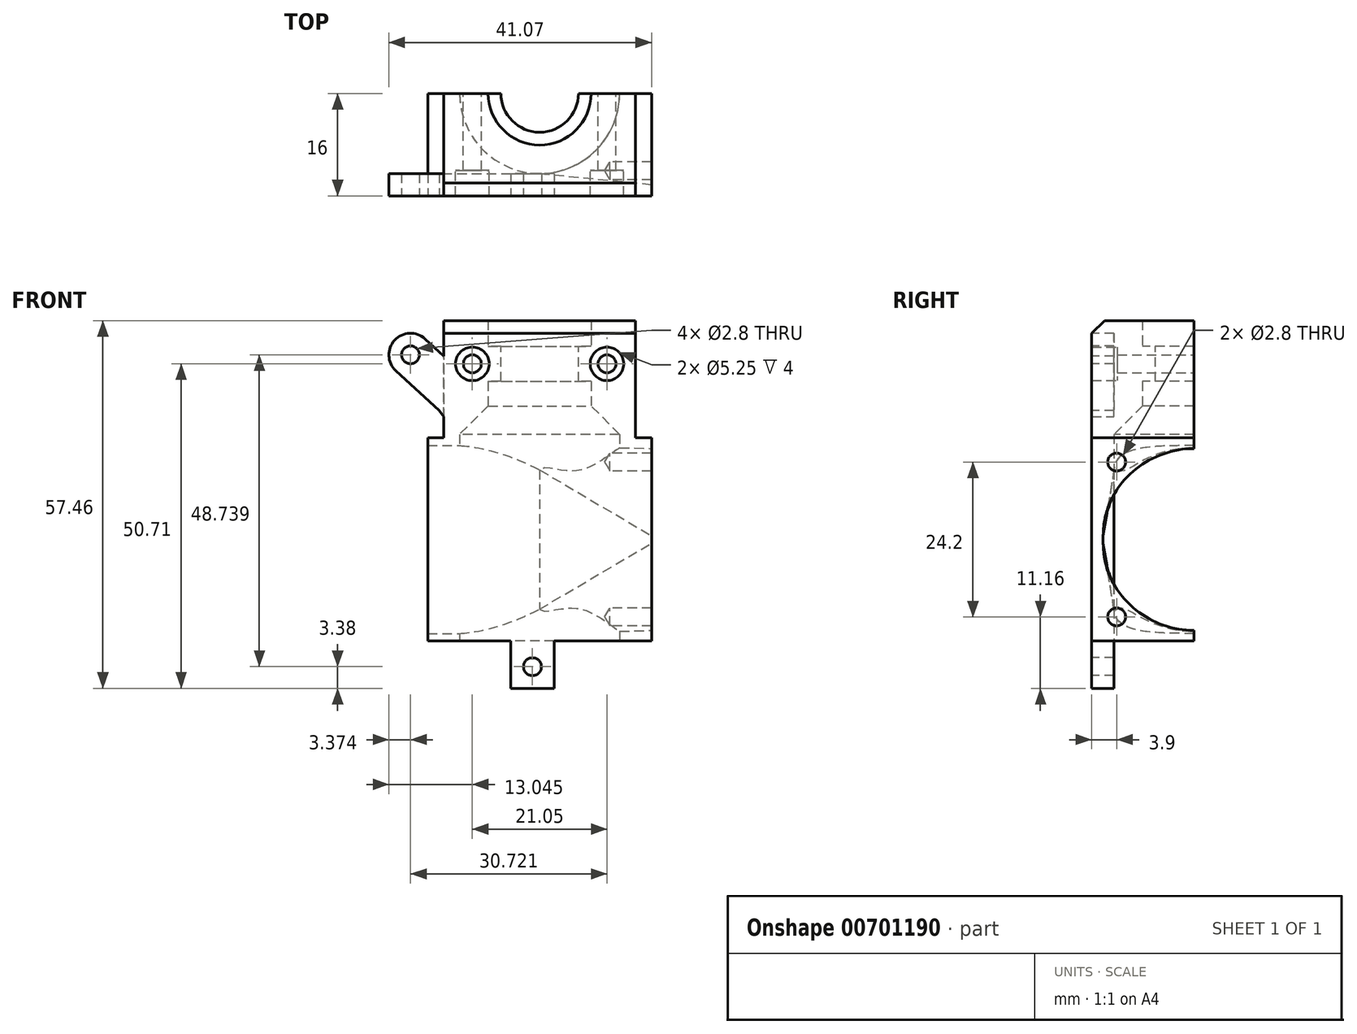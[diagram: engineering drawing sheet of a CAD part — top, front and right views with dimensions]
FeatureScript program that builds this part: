
annotation { "Feature Type Name" : "Feature", "Feature Type Description" : "" }
export const myFeature = defineFeature(function(context is Context, id is Id, definition is map)
    precondition{}
    {
        {
            var Q0;
            Q0=qCreatedBy(makeId("Front.planeOp"),FACE);
            var sketch = newSketch(context, id + "F0", { "sketchPlane" : qUnion([Q0])});
            skPoint(sketch, "E0.middle", {"position": v(0, 0) * mm});
            skLineSegment(sketch, "E1.bottom", {"start": v(17.5, 19.76) * mm, "end": v(-17.5, 19.76) * mm});
            skLineSegment(sketch, "E1.top", {"start": v(17.5, -12) * mm, "end": v(-17.5, -12) * mm});
            skLineSegment(sketch, "E1.left", {"start": v(17.5, 19.76) * mm, "end": v(17.5, -12) * mm});
            skLineSegment(sketch, "E1.right", {"start": v(-17.5, 19.76) * mm, "end": v(-17.5, -12) * mm});
            skLineSegment(sketch, "E2", {"start": v(-15, 19.76) * mm, "end": v(-15, 38.08) * mm});
            skLineSegment(sketch, "E3", {"start": v(-15, 38.08) * mm, "end": v(15, 38.08) * mm});
            skLineSegment(sketch, "E4", {"start": v(15, 38.08) * mm, "end": v(15, 19.76) * mm});
            skSolve(sketch);
        }
        {
            var Q0;
            Q0=makeQuery(id+"F0.imprint","IMPRINT",FACE,{"disambiguationData":[TD([[makeQuery(id+"F0.imprint","IMPRINT",EDGE,{"derivedFrom":sQuery(id+"F0.wireOp",EDGE,"E1.top")}),-1.0]])]});
            extrude(context, id + "F1", {"entities" : qUnion([Q0]), "oppositeDirection" : true, "depth" : 15 * mm, "offsetDistance" : 25 * mm});
        }
        {
            var Q0;
            Q0=makeQuery(id+"F1.opExtrude","SWEPT_FACE",FACE,{"disambiguationData":[OSD([sQuery(id+"F0.wireOp",EDGE,"E1.top")])]});
            var sketch = newSketch(context, id + "F2", { "sketchPlane" : qUnion([Q0])});
            skCircle(sketch, "E5", {"center": v(0, -15) * mm, "radius": 12.5 * mm});
            skSolve(sketch);
        }
        {
            var Q0;
            {var subQ0=sQuery(id+"F2.wireOp",EDGE,"E5");var subQ1=makeQuery(id+"F1.opExtrude","CAP_EDGE",EDGE,{"disambiguationData":[OSD([sQuery(id+"F0.wireOp",EDGE,"E1.top")])],"isStart":false});var subQ2=makeQuery(id+"F2.imprint","INTERSECT",VERTEX,{"disambiguationData":[OD(0.0)],"derivedFrom":[subQ1,subQ0]});Q0=makeQuery(id+"F2.imprint","IMPRINT",FACE,{"disambiguationData":[TD([[makeQuery(id+"F2.imprint","IMPRINT",EDGE,{"disambiguationData":[TD([[subQ2,-1.0]])],"derivedFrom":subQ0}),1.0]])]});}
            extrude(context, id + "F3", {"entities" : qUnion([Q0]), "operationType" : NewBodyOperationType.REMOVE, "endBound" : BoundingType.UP_TO_NEXT, "oppositeDirection" : true, "depth" : 25 * mm, "offsetDistance" : 25 * mm});
        }
        {
            var Q0;
            Q0=makeQuery(id+"F1.opExtrude","SWEPT_FACE",FACE,{"disambiguationData":[OSD([sQuery(id+"F0.wireOp",EDGE,"E1.right")])]});
            var sketch = newSketch(context, id + "F4", { "sketchPlane" : qUnion([Q0])});
            skFitSpline(sketch, "E6", {"points": [v(-15, -10.34) * mm, v(-0.79, 3.3) * mm], "startDerivative": vector(24.5, -0.23) * mm, "endDerivative": vector(0.56, 21.78) * mm});
            skFitSpline(sketch, "E7", {"points": [v(-15, 18.09) * mm, v(-0.79, 4.46) * mm], "startDerivative": vector(24.5, 0.26) * mm, "endDerivative": vector(0.56, -21.78) * mm});
            skLineSegment(sketch, "E8", {"start": v(-0.79, 4.46) * mm, "end": v(-0.79, 3.3) * mm});
            skLineSegment(sketch, "E9", {"start": v(-15, 3.88) * mm, "end": v(14.77, 3.88) * mm, "construction": true});
            skPoint(sketch, "E10", {"position": v(-2.9, 15.98) * mm});
            skPoint(sketch, "E11", {"position": v(-2.9, -8.22) * mm});
            skLineSegment(sketch, "E12", {"start": v(2.47, 18.88) * mm, "end": v(-9.32, 18.88) * mm, "construction": true});
            skLineSegment(sketch, "E13", {"start": v(1.95, -11.12) * mm, "end": v(-8.75, -11.12) * mm, "construction": true});
            skSolve(sketch);
        }
        {
            var Q0;
            Q0=makeQuery(id+"F1.opExtrude","SWEPT_FACE",FACE,{"disambiguationData":[OSD([sQuery(id+"F0.wireOp",EDGE,"E1.left")])]});
            var sketch = newSketch(context, id + "F5", { "sketchPlane" : qUnion([Q0])});
            skLineSegment(sketch, "E14", {"start": v(-4.6, 3.88) * mm, "end": v(19.4, 3.88) * mm, "construction": true});
            skLineSegment(sketch, "E15", {"start": v(-4.6, 18.88) * mm, "end": v(19.4, 18.88) * mm, "construction": true});
            skLineSegment(sketch, "E16", {"start": v(-4.6, -11.12) * mm, "end": v(19.4, -11.12) * mm, "construction": true});
            skLineSegment(sketch, "E17", {"start": v(0.79, 4.46) * mm, "end": v(0.79, 3.3) * mm});
            skFitSpline(sketch, "E18", {"points": [v(15, 18.1) * mm, v(0.79, 4.46) * mm], "startDerivative": vector(-21.58, 0) * mm, "endDerivative": vector(0, -24.08) * mm});
            skFitSpline(sketch, "E19", {"points": [v(0.79, 3.3) * mm, v(15, -10.33) * mm], "startDerivative": vector(0, -24.08) * mm, "endDerivative": vector(21.58, 0) * mm});
            skPoint(sketch, "E20", {"position": v(2.9, 15.98) * mm});
            skPoint(sketch, "E21", {"position": v(2.9, -8.22) * mm});
            skSolve(sketch);
        }
        {
            var Q0;
            {var subQ3=sQuery(id+"F4.wireOp",EDGE,"E6");Q0=makeQuery(id+"F4.imprint","IMPRINT",FACE,{"disambiguationData":[TD([[makeQuery(id+"F4.imprint","IMPRINT",EDGE,{"derivedFrom":subQ3}),-1.0]])]});}
            cPlane(context, id + "F6", {"entities" : qUnion([Q0]), "cplaneType" : CPlaneType.OFFSET, "offset" : 17.5 * mm, "oppositeDirection" : true, "width" : 150 * mm, "height" : 150 * mm});
        }
        {
            var Q0;
            Q0=qCreatedBy(id+"F6.planeOp",FACE);
            var sketch = newSketch(context, id + "F7", { "sketchPlane" : qUnion([Q0])});
            skFitSpline(sketch, "E22", {"points": [v(-15, -10.8) * mm, v(-2.5, -7) * mm], "startDerivative": vector(18.69, 0) * mm, "endDerivative": vector(0, 11.4) * mm});
            skLineSegment(sketch, "E23", {"start": v(-8.77, -11.88) * mm, "end": v(-8.77, 19.6) * mm, "construction": true});
            skFitSpline(sketch, "E24", {"points": [v(-15, 18.55) * mm, v(-2.5, 14.75) * mm], "startDerivative": vector(18.69, 0) * mm, "endDerivative": vector(0, -11.4) * mm});
            skLineSegment(sketch, "E25", {"start": v(-2.5, 20.58) * mm, "end": v(-2.5, -14.77) * mm, "construction": true});
            skLineSegment(sketch, "E26", {"start": v(-2.5, 14.75) * mm, "end": v(-2.5, -7) * mm});
            skLineSegment(sketch, "E27", {"start": v(-15, -10.8) * mm, "end": v(-15, 18.55) * mm});
            skSolve(sketch);
        }
        {
            var Q0;
            Q0=makeQuery(id+"F7.imprint","IMPRINT",FACE,{"disambiguationData":[TD([[makeQuery(id+"F7.imprint","IMPRINT",EDGE,{"derivedFrom":sQuery(id+"F7.wireOp",EDGE,"E22")}),1.0]])]});
            var Q1;
            Q1=makeQuery(id+"F5.imprint","IMPRINT",FACE,{"disambiguationData":[TD([[makeQuery(id+"F5.imprint","IMPRINT",EDGE,{"derivedFrom":sQuery(id+"F5.wireOp",EDGE,"E17")}),1.0]])]});
            loft(context, id + "F8", {"operationType" : NewBodyOperationType.REMOVE, "sheetProfilesArray" : [{ "sheetProfileEntities" : qUnion([Q0]) }, { "sheetProfileEntities" : qUnion([Q1]) }]});
        }
        {
            var Q0;
            Q0=qSketchRegion(id+"F7",true);
            extrude(context, id + "F9", {"entities" : qUnion([Q0]), "operationType" : NewBodyOperationType.REMOVE, "depth" : 30 * mm, "offsetDistance" : 25 * mm});
        }
        {
            var Q0;
            Q0=qSketchRegion(id+"F0",true);
            extrude(context, id + "F10", {"entities" : qUnion([Q0]), "operationType" : NewBodyOperationType.ADD, "depth" : 1 * mm, "offsetDistance" : 25 * mm});
        }
        {
            var Q0;
            Q0=sQuery(id+"F5.wireOp",VERTEX,"E20");
            var Q1;
            Q1=sQuery(id+"F5.wireOp",VERTEX,"E21");
            var Q2;
            Q2=makeQuery(id+"F1.opExtrude","SWEPT_BODY",BODY,{"disambiguationData":[OSD([sQuery(id+"F0.wireOp",EDGE,"olvQiCSQ-iVDM-BvRe-21EI-2ykU3FyUineD"),sQuery(id+"F0.wireOp",EDGE,"tQqsZeP7-s7as-o93x-ybZ7-DSYlx5VF5dZE"),sQuery(id+"F0.wireOp",EDGE,"E1.bottom"),sQuery(id+"F0.wireOp",EDGE,"E1.top"),sQuery(id+"F0.wireOp",EDGE,"E1.left"),sQuery(id+"F0.wireOp",EDGE,"E1.right")])]});
            hole(context, id + "F11", {"style" : HoleStyle.SIMPLE, "endStyle" : HoleEndStyle.BLIND, "holeDiameter" : 2.8 * mm, "majorDiameter" : 5 * mm, "holeDepth" : 6.5 * mm, "isTappedThrough" : true, "tappedDepth" : 12 * mm, "tapClearance" : 3, "locations" : qUnion([Q0, Q1]), "scope" : qUnion([Q2]), "startStyle" : HoleStartStyle.PART});
        }
        {
            var Q0;
            Q0=makeQuery(id+"F10.opExtrude","SWEPT_FACE",FACE,{"disambiguationData":[OSD([sQuery(id+"F0.wireOp",EDGE,"E3")])]});
            cPlane(context, id + "F12", {"entities" : qUnion([Q0]), "cplaneType" : CPlaneType.OFFSET, "offset" : 18.32 * mm, "oppositeDirection" : true, "width" : 150 * mm, "height" : 150 * mm});
        }
        {
            var Q0;
            Q0=qCreatedBy(id+"F12.planeOp",FACE);
            var sketch = newSketch(context, id + "F13", { "sketchPlane" : qUnion([Q0])});
            skLineSegment(sketch, "E28.bottom", {"start": v(-15, 0) * mm, "end": v(15, 0) * mm});
            skLineSegment(sketch, "E28.top", {"start": v(-15, 15) * mm, "end": v(15, 15) * mm});
            skLineSegment(sketch, "E28.left", {"start": v(-15, 0) * mm, "end": v(-15, 15) * mm});
            skLineSegment(sketch, "E28.right", {"start": v(15, 0) * mm, "end": v(15, 15) * mm});
            skCircle(sketch, "E29", {"center": v(0, 15) * mm, "radius": 8.05 * mm});
            skCircle(sketch, "E30", {"center": v(0, 15) * mm, "radius": 6.05 * mm});
            skSolve(sketch);
        }
        {
            var Q0;
            Q0=makeQuery(id+"F13.imprint","IMPRINT",FACE,{"disambiguationData":[TD([[makeQuery(id+"F13.imprint","IMPRINT",EDGE,{"derivedFrom":sQuery(id+"F13.wireOp",EDGE,"E28.bottom")}),1.0]])]});
            extrude(context, id + "F14", {"entities" : qUnion([Q0]), "operationType" : NewBodyOperationType.ADD, "depth" : 18.32 * mm, "offsetDistance" : 25 * mm});
        }
        {
            var Q0;
            Q0=makeQuery(id+"F14.boolean.opBoolean","MERGE",FACE,{"derivedFrom":[makeQuery(id+"F10.opExtrude","SWEPT_FACE",FACE,{"disambiguationData":[OSD([sQuery(id+"F0.wireOp",EDGE,"E3")])]}),makeQuery(id+"F14.opExtrude","CAP_FACE",FACE,{"disambiguationData":[OSD([sQuery(id+"F13.wireOp",EDGE,"E28.bottom"),sQuery(id+"F13.wireOp",EDGE,"E28.top"),sQuery(id+"F13.wireOp",EDGE,"E28.left"),sQuery(id+"F13.wireOp",EDGE,"E28.right"),sQuery(id+"F13.wireOp",EDGE,"E29")])],"isStart":false})]});
            cPlane(context, id + "F15", {"entities" : qUnion([Q0]), "cplaneType" : CPlaneType.OFFSET, "offset" : 4 * mm, "oppositeDirection" : true, "width" : 150 * mm, "height" : 150 * mm});
        }
        {
            var Q0;
            Q0=qCreatedBy(id+"F15.planeOp",FACE);
            var sketch = newSketch(context, id + "F16", { "sketchPlane" : qUnion([Q0])});
            skCircle(sketch, "E31", {"center": v(0, 15) * mm, "radius": 6.05 * mm});
            skCircle(sketch, "E32", {"center": v(0, 15) * mm, "radius": 8.05 * mm});
            skLineSegment(sketch, "E33", {"start": v(0, 0) * mm, "end": v(12, 0) * mm});
            skLineSegment(sketch, "E34", {"start": v(12, 0) * mm, "end": v(12, 15) * mm});
            skLineSegment(sketch, "E35", {"start": v(12, 15) * mm, "end": v(-12, 15) * mm});
            skLineSegment(sketch, "E36", {"start": v(-12, 15) * mm, "end": v(-12, 0) * mm});
            skLineSegment(sketch, "E37", {"start": v(-12, 0) * mm, "end": v(0, 0) * mm});
            skSolve(sketch);
        }
        {
            var Q0;
            {var subQ0=sQuery(id+"F16.wireOp",EDGE,"E35");var subQ1=sQuery(id+"F16.wireOp",EDGE,"E31");var subQ2=makeQuery(id+"F16.imprint","INTERSECT",VERTEX,{"disambiguationData":[OD(0.0)],"derivedFrom":[subQ1,subQ0]});Q0=makeQuery(id+"F16.imprint","IMPRINT",FACE,{"disambiguationData":[TD([[makeQuery(id+"F16.imprint","IMPRINT",EDGE,{"disambiguationData":[TD([[subQ2,1.0]])],"derivedFrom":subQ1}),-1.0]])]});}
            extrude(context, id + "F17", {"entities" : qUnion([Q0]), "operationType" : NewBodyOperationType.ADD, "oppositeDirection" : true, "depth" : 5.5 * mm, "offsetDistance" : 25 * mm});
        }
        {
            var Q0;
            Q0=makeQuery(id+"F10.opExtrude","CAP_FACE",FACE,{"disambiguationData":[OSD([sQuery(id+"F0.wireOp",EDGE,"E1.top"),sQuery(id+"F0.wireOp",EDGE,"E1.left"),sQuery(id+"F0.wireOp",EDGE,"E1.right"),sQuery(id+"F0.wireOp",EDGE,"E1.bottom"),sQuery(id+"F0.wireOp",EDGE,"E2"),sQuery(id+"F0.wireOp",EDGE,"E3"),sQuery(id+"F0.wireOp",EDGE,"E4")])],"isStart":false});
            var sketch = newSketch(context, id + "F18", { "sketchPlane" : qUnion([Q0])});
            skPoint(sketch, "E38", {"position": v(10.52, 31.33) * mm});
            skPoint(sketch, "E39", {"position": v(-10.53, 31.33) * mm});
            skLineSegment(sketch, "E40", {"start": v(15, 31.33) * mm, "end": v(6.05, 31.33) * mm, "construction": true});
            skLineSegment(sketch, "E41", {"start": v(-15, 31.33) * mm, "end": v(-6.05, 31.33) * mm, "construction": true});
            skSolve(sketch);
        }
        {
            var Q0;
            Q0=sQuery(id+"F18.wireOp",VERTEX,"E38");
            var Q1;
            Q1=sQuery(id+"F18.wireOp",VERTEX,"E39");
            var Q2;
            Q2=makeQuery(id+"F1.opExtrude","SWEPT_BODY",BODY,{"disambiguationData":[OSD([sQuery(id+"F0.wireOp",EDGE,"olvQiCSQ-iVDM-BvRe-21EI-2ykU3FyUineD"),sQuery(id+"F0.wireOp",EDGE,"tQqsZeP7-s7as-o93x-ybZ7-DSYlx5VF5dZE"),sQuery(id+"F0.wireOp",EDGE,"E1.top"),sQuery(id+"F0.wireOp",EDGE,"E1.left"),sQuery(id+"F0.wireOp",EDGE,"E1.right"),sQuery(id+"F0.wireOp",EDGE,"E1.bottom")])]});
            hole(context, id + "F19", {"style" : HoleStyle.C_BORE, "endStyle" : HoleEndStyle.BLIND, "holeDiameter" : 2.8 * mm, "cBoreDiameter" : 5.25 * mm, "cBoreDepth" : 4 * mm, "majorDiameter" : 5 * mm, "holeDepth" : 20 * mm, "isTappedThrough" : true, "tappedDepth" : 12 * mm, "tapClearance" : 3, "locations" : qUnion([Q0, Q1]), "scope" : qUnion([Q2]), "startStyle" : HoleStartStyle.PART});
        }
        {
            var Q0;
            Q0=makeQuery(id+"F10.opExtrude","CAP_EDGE",EDGE,{"disambiguationData":[OSD([sQuery(id+"F0.wireOp",EDGE,"E3")])],"isStart":false});
            chamfer(context, id + "F20", {"entities" : qUnion([Q0]), "width" : 2 * mm, "tangentPropagation" : true});
        }
        {
            var Q0;
            Q0=makeQuery(id+"F14.opExtrude","CAP_EDGE",EDGE,{"disambiguationData":[OSD([sQuery(id+"F13.wireOp",EDGE,"E29")])],"isStart":true});
            var Q1;
            Q1=makeQuery(id+"F14.opExtrude","CAP_EDGE",EDGE,{"disambiguationData":[OSD([sQuery(id+"F13.wireOp",EDGE,"E28.right")])],"isStart":true});
            var Q2;
            Q2=makeQuery(id+"F14.opExtrude","CAP_EDGE",EDGE,{"disambiguationData":[OSD([sQuery(id+"F13.wireOp",EDGE,"E28.left")])],"isStart":true});
            chamfer(context, id + "F21", {"entities" : qUnion([Q0, Q1, Q2]), "width" : 5 * mm, "tangentPropagation" : true});
        }
        {
            var Q0;
            Q0=makeQuery(id+"F18.imprint","IMPRINT",FACE,{"disambiguationData":[TD([[makeQuery(id+"F18.imprint","IMPRINT",EDGE,{"derivedFrom":makeQuery(id+"F10.opExtrude","CAP_EDGE",EDGE,{"disambiguationData":[OSD([sQuery(id+"F0.wireOp",EDGE,"E1.top")])],"isStart":false})}),-1.0]])]});
            var sketch = newSketch(context, id + "F22", { "sketchPlane" : qUnion([Q0])});
            skLineSegment(sketch, "E42", {"start": v(-15, 32.56) * mm, "end": v(-17.92, 35.23) * mm});
            skLineSegment(sketch, "E43", {"start": v(-22.47, 30.25) * mm, "end": v(-15.7, 24.06) * mm});
            skCircle(sketch, "E44", {"center": v(-20.2, 32.74) * mm, "radius": 3.37 * mm});
            skPoint(sketch, "E44.third.point", {"position": v(-22.47, 35.23) * mm});
            skCircle(sketch, "E45", {"center": v(-20.2, 32.74) * mm, "radius": 1.4 * mm});
            skLineSegment(sketch, "E46.bottom", {"start": v(2.25, -12) * mm, "end": v(-4.5, -12) * mm});
            skLineSegment(sketch, "E46.top", {"start": v(2.25, -16) * mm, "end": v(-4.5, -16) * mm});
            skLineSegment(sketch, "E46.left", {"start": v(2.25, -12) * mm, "end": v(2.25, -16) * mm});
            skLineSegment(sketch, "E46.right", {"start": v(-4.5, -12) * mm, "end": v(-4.5, -16) * mm});
            skCircle(sketch, "E47", {"center": v(-1.12, -16) * mm, "radius": 3.38 * mm});
            skCircle(sketch, "E48", {"center": v(-1.12, -16) * mm, "radius": 1.4 * mm});
            skLineSegment(sketch, "E49", {"start": v(-15, 32.56) * mm, "end": v(-13.55, 27.77) * mm});
            skLineSegment(sketch, "E50", {"start": v(-13.55, 27.77) * mm, "end": v(-14.85, 22.84) * mm});
            skLineSegment(sketch, "E51", {"start": v(-14.85, 22.84) * mm, "end": v(-15.7, 24.06) * mm});
            skLineSegment(sketch, "E52.bottom", {"start": v(-4.5, -16) * mm, "end": v(2.25, -16) * mm});
            skLineSegment(sketch, "E52.top", {"start": v(-4.5, -19.38) * mm, "end": v(2.25, -19.38) * mm});
            skLineSegment(sketch, "E52.left", {"start": v(-4.5, -16) * mm, "end": v(-4.5, -19.38) * mm});
            skLineSegment(sketch, "E52.right", {"start": v(2.25, -16) * mm, "end": v(2.25, -19.38) * mm});
            skSolve(sketch);
        }
        {
            var Q0;
            Q0 = qSketchRegion(id + "F22", true);
            extrude(context, id + "F23", {"entities" : qUnion([Q0]), "operationType" : NewBodyOperationType.ADD, "oppositeDirection" : true, "depth" : 3.5 * mm, "offsetDistance" : 25 * mm});
        }
    });
